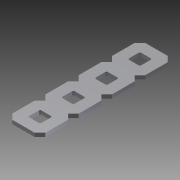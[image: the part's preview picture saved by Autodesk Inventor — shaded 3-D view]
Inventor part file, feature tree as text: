
AUTODESK INVENTOR PART (.ipt)
format: ipt  version: 2014 SP1 (Build 180222100, 222)  size: 478,208 bytes
history: native  units: in
note: dims shown in document units (in); Inventor stores cm internally (conversion verified against a paired STEP export)
features: other x1, imported_body x1, extrude x1, sketch x1
ambient origin geometry x8: Origin, YZ Plane, XZ Plane, XY Plane, X Axis, Y Axis, Z Axis, Center Point
bodies: Body1 (feature_tree)
feature tree (4):
  parser-record x1  (decoder bookkeeping rows leaked as tree rows — omitted from the tree; the rows remain in map.json)
  imported_body  "Base1"
  extrude  "Extrusion1"  Depth=1.0in TaperAngle=0.0deg
  sketch  "Sketch1"  dims[d0=2.0in d1=1.0in d2=0.0in]
